# Revit family: 94879- forno touch
name_source: partatom
category: Equipamento especial
revit_build: Autodesk Revit 2016 (Build: 20150220_1215(x64)
units: mm (PartAtom-declared; Revit-internal decimal feet)

## family parameters
Com base no plano de trabalho = Não
Compartilhado = Não
Corte com vazios quando carregados = Não
Cota do conector redondo = Utilizar diâmetro
Ponto de cálculo do ambiente = Não
Sempre na vertical = Sim
Tipo de parte = Normal

## types (1)
- Tramontina Forno Elétrico - 94879
    Acessorios = 2 grelhas e 2 bandejas
    Código de montagem = 94879/220
    Descrição = 94879/220
    Desenvolvedor = Factory Cursos & Desenvolvimento
    Fabricante = Tramontina
    Frequência = 60 Hz
    Modelo = Slim Touch 60 F12
    Nicho para instalação (AxLxP) = 590 X 560 X 600
    Potência  "Grill" = 1050 W
    Potência "Aquecimento Inferior" = 1150 W
    Potência "Aquecimento Superior Combinado" = 2090 W
    Potência "Aquecimento superior" = 2070 MHz
    Potência "Assar Combinado" = 2100 W
    Potência "Assar" = 2160 W
    Potência "Booster" = 2800 W
    Potência "Descongelamento " = 21 W
    Potência "Manter Aquecimento" = 1720 W
    Potência "Multicozimento" = 1900 W
    Potência "Turbo Aquecimento Combinado" = 2800 W
    Potência "Turbo Aquecimento Slow" - Préaquecimento = 2720 W
    Potência "Turbo Aquecimento Slow" -Cozimento = 1720 W
    Potência "Turbo Aquecimento" = 1710 W
    Potência Elétrica total = 2800 W
    Site do desenvolvedor = www.factorycursos.com.br
    Temperatura máxima do forno = 280°
    Tensão = 220 V
    URL = www.tramontina.com.br

## geometry (parser evidence)
native form markers: Blend x12
no freeform markers — native parametric forms only
